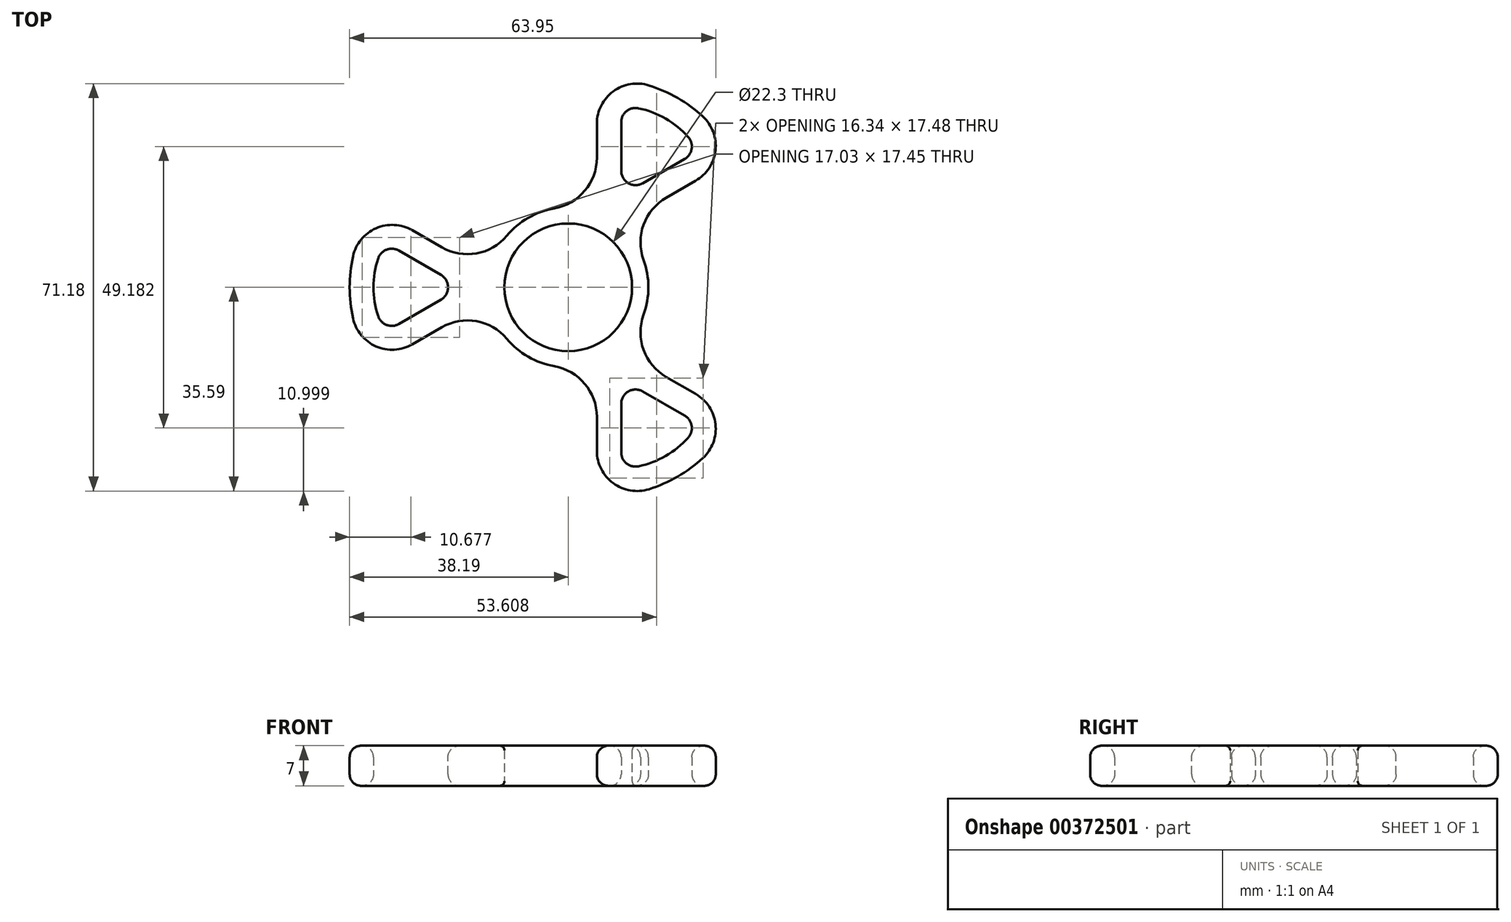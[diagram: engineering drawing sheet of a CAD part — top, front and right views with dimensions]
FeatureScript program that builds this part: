
annotation { "Feature Type Name" : "Feature", "Feature Type Description" : "" }
export const myFeature = defineFeature(function(context is Context, id is Id, definition is map)
    precondition{}
    {
        {
            var Q0;
            Q0=qCreatedBy(makeId("Top.planeOp"),FACE);
            var sketch = newSketch(context, id + "F0", { "sketchPlane" : qUnion([Q0])});
            skArc(sketch, "E0", {"start": v(-13.82, -2.2) * mm, "mid": v(-7, -12.12) * mm, "end": v(5, -13.08) * mm});
            skCircle(sketch, "E1.cCircle", {"center": v(-26, 0) * mm, "radius": 16 * mm, "construction": true});
            skLineSegment(sketch, "E1.0", {"start": v(-13.82, -2.2) * mm, "end": v(-34, -13.86) * mm});
            skLineSegment(sketch, "E1.2", {"start": v(-34, 13.86) * mm, "end": v(-13.82, 2.2) * mm});
            skPoint(sketch, "E2.orphan", {"position": v(-10, 0) * mm});
            skPoint(sketch, "E3.orphan", {"position": v(10, 0) * mm});
            skArc(sketch, "E4.trimOffspring", {"start": v(14, 0) * mm, "mid": v(12.64, 6.02) * mm, "end": v(8.82, 10.87) * mm});
            skArc(sketch, "E5", {"start": v(-34, 13.86) * mm, "mid": v(-38.2, 0) * mm, "end": v(-34, -13.86) * mm});
            skCircle(sketch, "E6", {"center": v(0, 0) * mm, "radius": 11.15 * mm});
            skCircle(sketch, "E7.cCircle", {"center": v(-27.5, 0) * mm, "radius": 9 * mm, "construction": true});
            skLineSegment(sketch, "E7.0", {"start": v(-18.5, 0) * mm, "end": v(-32, -7.8) * mm});
            skLineSegment(sketch, "E7.2", {"start": v(-32, 7.8) * mm, "end": v(-18.5, 0) * mm});
            skArc(sketch, "E8", {"start": v(-32, 7.8) * mm, "mid": v(-34.03, 0) * mm, "end": v(-32, -7.8) * mm});
            skLineSegment(sketch, "E9.1.0", {"start": v(9.25, -31.6) * mm, "end": v(9.25, -16.02) * mm});
            skCircle(sketch, "E9.1.1", {"center": v(13.75, -23.82) * mm, "radius": 9 * mm, "construction": true});
            skArc(sketch, "E9.1.2", {"start": v(9.25, -31.6) * mm, "mid": v(17.01, -29.47) * mm, "end": v(22.75, -23.82) * mm});
            skArc(sketch, "E9.1.3", {"start": v(5, -36.37) * mm, "mid": v(19.1, -33.07) * mm, "end": v(29, -22.52) * mm});
            skLineSegment(sketch, "E9.1.4", {"start": v(9.25, -16.02) * mm, "end": v(22.75, -23.82) * mm});
            skLineSegment(sketch, "E9.1.5", {"start": v(5, -36.37) * mm, "end": v(5, -13.08) * mm});
            skLineSegment(sketch, "E9.1.6", {"start": v(8.82, -10.87) * mm, "end": v(29, -22.52) * mm});
            skCircle(sketch, "E9.1.7", {"center": v(13, -22.52) * mm, "radius": 16 * mm, "construction": true});
            skLineSegment(sketch, "E9.2.0", {"start": v(22.75, 23.82) * mm, "end": v(9.25, 16.02) * mm});
            skCircle(sketch, "E9.2.1", {"center": v(13.75, 23.82) * mm, "radius": 9 * mm, "construction": true});
            skArc(sketch, "E9.2.2", {"start": v(22.75, 23.82) * mm, "mid": v(17.01, 29.47) * mm, "end": v(9.25, 31.6) * mm});
            skArc(sketch, "E9.2.3", {"start": v(29, 22.52) * mm, "mid": v(19.1, 33.07) * mm, "end": v(5, 36.37) * mm});
            skLineSegment(sketch, "E9.2.4", {"start": v(9.25, 16.02) * mm, "end": v(9.25, 31.6) * mm});
            skLineSegment(sketch, "E9.2.5", {"start": v(29, 22.52) * mm, "end": v(8.82, 10.87) * mm});
            skLineSegment(sketch, "E9.2.6", {"start": v(5, 13.08) * mm, "end": v(5, 36.37) * mm});
            skCircle(sketch, "E9.2.7", {"center": v(13, 22.52) * mm, "radius": 16 * mm, "construction": true});
            skArc(sketch, "E10.trimOffspring", {"start": v(5, 13.08) * mm, "mid": v(-7, 12.12) * mm, "end": v(-13.82, 2.2) * mm});
            skArc(sketch, "E11.trimOffspring", {"start": v(8.82, -10.87) * mm, "mid": v(12.64, -6.02) * mm, "end": v(14, 0) * mm});
            skSolve(sketch);
        }
        {
            var Q0;
            Q0=qSketchRegion(id+"F0",true);
            extrude(context, id + "F1", {"entities" : qUnion([Q0]), "depth" : 7 * mm});
        }
        {
            var Q0;
            Q0=makeQuery(id+"F1.opExtrude","SWEPT_EDGE",EDGE,{"disambiguationData":[OSD([sQuery(id+"F0.wireOp",EDGE,"E0"),sQuery(id+"F0.wireOp",EDGE,"E1.0")])]});
            var Q1;
            Q1=makeQuery(id+"F1.opExtrude","SWEPT_EDGE",EDGE,{"disambiguationData":[OSD([sQuery(id+"F0.wireOp",EDGE,"E0"),sQuery(id+"F0.wireOp",EDGE,"E9.1.5")])]});
            var Q2;
            Q2=makeQuery(id+"F1.opExtrude","SWEPT_EDGE",EDGE,{"disambiguationData":[OSD([sQuery(id+"F0.wireOp",EDGE,"E9.1.6"),sQuery(id+"F0.wireOp",EDGE,"E11.trimOffspring")])]});
            var Q3;
            Q3=makeQuery(id+"F1.opExtrude","SWEPT_EDGE",EDGE,{"disambiguationData":[OSD([sQuery(id+"F0.wireOp",EDGE,"E4.trimOffspring"),sQuery(id+"F0.wireOp",EDGE,"E9.2.5")])]});
            var Q4;
            Q4=makeQuery(id+"F1.opExtrude","SWEPT_EDGE",EDGE,{"disambiguationData":[OSD([sQuery(id+"F0.wireOp",EDGE,"E9.2.6"),sQuery(id+"F0.wireOp",EDGE,"E10.trimOffspring")])]});
            var Q5;
            Q5=makeQuery(id+"F1.opExtrude","SWEPT_EDGE",EDGE,{"disambiguationData":[OSD([sQuery(id+"F0.wireOp",EDGE,"E1.2"),sQuery(id+"F0.wireOp",EDGE,"E10.trimOffspring")])]});
            fillet(context, id + "F2", {"entities" : qUnion([Q0, Q1, Q2, Q3, Q4, Q5]), "radius" : 9 * mm, "tangentPropagation" : true, "allowEdgeOverflow" : false});
        }
        {
            var Q0;
            Q0=makeQuery(id+"F1.opExtrude","SWEPT_EDGE",EDGE,{"disambiguationData":[OSD([sQuery(id+"F0.wireOp",EDGE,"E9.1.3"),sQuery(id+"F0.wireOp",EDGE,"E9.1.6")])]});
            var Q1;
            Q1=makeQuery(id+"F1.opExtrude","SWEPT_EDGE",EDGE,{"disambiguationData":[OSD([sQuery(id+"F0.wireOp",EDGE,"E9.2.3"),sQuery(id+"F0.wireOp",EDGE,"E9.2.5")])]});
            var Q2;
            Q2=makeQuery(id+"F1.opExtrude","SWEPT_EDGE",EDGE,{"disambiguationData":[OSD([sQuery(id+"F0.wireOp",EDGE,"E9.2.3"),sQuery(id+"F0.wireOp",EDGE,"E9.2.6")])]});
            var Q3;
            Q3=makeQuery(id+"F1.opExtrude","SWEPT_EDGE",EDGE,{"disambiguationData":[OSD([sQuery(id+"F0.wireOp",EDGE,"E1.2"),sQuery(id+"F0.wireOp",EDGE,"E5")])]});
            var Q4;
            Q4=makeQuery(id+"F1.opExtrude","SWEPT_EDGE",EDGE,{"disambiguationData":[OSD([sQuery(id+"F0.wireOp",EDGE,"E1.0"),sQuery(id+"F0.wireOp",EDGE,"E5")])]});
            var Q5;
            Q5=makeQuery(id+"F1.opExtrude","SWEPT_EDGE",EDGE,{"disambiguationData":[OSD([sQuery(id+"F0.wireOp",EDGE,"E9.1.3"),sQuery(id+"F0.wireOp",EDGE,"E9.1.5")])]});
            fillet(context, id + "F3", {"entities" : qUnion([Q0, Q1, Q2, Q3, Q4, Q5]), "radius" : 7 * mm, "tangentPropagation" : true, "defaultsChanged" : true, "vertexSettings" : [], "allowEdgeOverflow" : false});
        }
        {
            var Q0;
            Q0=makeQuery(id+"F1.opExtrude","SWEPT_EDGE",EDGE,{"disambiguationData":[OSD([sQuery(id+"F0.wireOp",EDGE,"E7.2"),sQuery(id+"F0.wireOp",EDGE,"E8")])]});
            var Q1;
            Q1=makeQuery(id+"F1.opExtrude","SWEPT_EDGE",EDGE,{"disambiguationData":[OSD([sQuery(id+"F0.wireOp",EDGE,"E7.0"),sQuery(id+"F0.wireOp",EDGE,"E7.2")])]});
            var Q2;
            Q2=makeQuery(id+"F1.opExtrude","SWEPT_EDGE",EDGE,{"disambiguationData":[OSD([sQuery(id+"F0.wireOp",EDGE,"E7.0"),sQuery(id+"F0.wireOp",EDGE,"E8")])]});
            var Q3;
            Q3=makeQuery(id+"F1.opExtrude","SWEPT_EDGE",EDGE,{"disambiguationData":[OSD([sQuery(id+"F0.wireOp",EDGE,"E9.1.0"),sQuery(id+"F0.wireOp",EDGE,"E9.1.2")])]});
            var Q4;
            Q4=makeQuery(id+"F1.opExtrude","SWEPT_EDGE",EDGE,{"disambiguationData":[OSD([sQuery(id+"F0.wireOp",EDGE,"E9.1.0"),sQuery(id+"F0.wireOp",EDGE,"E9.1.4")])]});
            var Q5;
            Q5=makeQuery(id+"F1.opExtrude","SWEPT_EDGE",EDGE,{"disambiguationData":[OSD([sQuery(id+"F0.wireOp",EDGE,"E9.1.2"),sQuery(id+"F0.wireOp",EDGE,"E9.1.4")])]});
            var Q6;
            Q6=makeQuery(id+"F1.opExtrude","SWEPT_EDGE",EDGE,{"disambiguationData":[OSD([sQuery(id+"F0.wireOp",EDGE,"E9.2.0"),sQuery(id+"F0.wireOp",EDGE,"E9.2.4")])]});
            var Q7;
            Q7=makeQuery(id+"F1.opExtrude","SWEPT_EDGE",EDGE,{"disambiguationData":[OSD([sQuery(id+"F0.wireOp",EDGE,"E9.2.2"),sQuery(id+"F0.wireOp",EDGE,"E9.2.4")])]});
            var Q8;
            Q8=makeQuery(id+"F1.opExtrude","SWEPT_EDGE",EDGE,{"disambiguationData":[OSD([sQuery(id+"F0.wireOp",EDGE,"E9.2.0"),sQuery(id+"F0.wireOp",EDGE,"E9.2.2")])]});
            fillet(context, id + "F4", {"entities" : qUnion([Q0, Q1, Q2, Q3, Q4, Q5, Q6, Q7, Q8]), "radius" : 2.5 * mm, "tangentPropagation" : true, "defaultsChanged" : true, "vertexSettings" : [], "allowEdgeOverflow" : false});
        }
        {
            var Q0;
            Q0=makeQuery(id+"F1.opExtrude","SWEPT_FACE",FACE,{"disambiguationData":[OSD([sQuery(id+"F0.wireOp",EDGE,"E6")])]});
            fillet(context, id + "F5", {"entities" : qUnion([Q0]), "radius" : .8 * mm, "tangentPropagation" : true, "allowEdgeOverflow" : false});
        }
        {
            var Q0;
            Q0=makeQuery(id+"F1.opExtrude","CAP_FACE",FACE,{"disambiguationData":[OSD([sQuery(id+"F0.wireOp",EDGE,"E0"),sQuery(id+"F0.wireOp",EDGE,"E1.0"),sQuery(id+"F0.wireOp",EDGE,"E1.2"),sQuery(id+"F0.wireOp",EDGE,"E4.trimOffspring"),sQuery(id+"F0.wireOp",EDGE,"E5"),sQuery(id+"F0.wireOp",EDGE,"E6"),sQuery(id+"F0.wireOp",EDGE,"E7.0"),sQuery(id+"F0.wireOp",EDGE,"E7.2"),sQuery(id+"F0.wireOp",EDGE,"E8"),sQuery(id+"F0.wireOp",EDGE,"E9.1.0"),sQuery(id+"F0.wireOp",EDGE,"E9.1.2"),sQuery(id+"F0.wireOp",EDGE,"E9.1.3"),sQuery(id+"F0.wireOp",EDGE,"E9.1.4"),sQuery(id+"F0.wireOp",EDGE,"E9.1.5"),sQuery(id+"F0.wireOp",EDGE,"E9.1.6"),sQuery(id+"F0.wireOp",EDGE,"E9.2.0"),sQuery(id+"F0.wireOp",EDGE,"E9.2.2"),sQuery(id+"F0.wireOp",EDGE,"E9.2.3"),sQuery(id+"F0.wireOp",EDGE,"E9.2.4"),sQuery(id+"F0.wireOp",EDGE,"E9.2.5"),sQuery(id+"F0.wireOp",EDGE,"E9.2.6"),sQuery(id+"F0.wireOp",EDGE,"E10.trimOffspring"),sQuery(id+"F0.wireOp",EDGE,"E11.trimOffspring")])],"isStart":false});
            var Q1;
            Q1=makeQuery(id+"F1.opExtrude","CAP_FACE",FACE,{"disambiguationData":[OSD([sQuery(id+"F0.wireOp",EDGE,"E0"),sQuery(id+"F0.wireOp",EDGE,"E1.0"),sQuery(id+"F0.wireOp",EDGE,"E1.2"),sQuery(id+"F0.wireOp",EDGE,"E4.trimOffspring"),sQuery(id+"F0.wireOp",EDGE,"E5"),sQuery(id+"F0.wireOp",EDGE,"E6"),sQuery(id+"F0.wireOp",EDGE,"E7.0"),sQuery(id+"F0.wireOp",EDGE,"E7.2"),sQuery(id+"F0.wireOp",EDGE,"E8"),sQuery(id+"F0.wireOp",EDGE,"E9.1.0"),sQuery(id+"F0.wireOp",EDGE,"E9.1.2"),sQuery(id+"F0.wireOp",EDGE,"E9.1.3"),sQuery(id+"F0.wireOp",EDGE,"E9.1.4"),sQuery(id+"F0.wireOp",EDGE,"E9.1.5"),sQuery(id+"F0.wireOp",EDGE,"E9.1.6"),sQuery(id+"F0.wireOp",EDGE,"E9.2.0"),sQuery(id+"F0.wireOp",EDGE,"E9.2.2"),sQuery(id+"F0.wireOp",EDGE,"E9.2.3"),sQuery(id+"F0.wireOp",EDGE,"E9.2.4"),sQuery(id+"F0.wireOp",EDGE,"E9.2.5"),sQuery(id+"F0.wireOp",EDGE,"E9.2.6"),sQuery(id+"F0.wireOp",EDGE,"E10.trimOffspring"),sQuery(id+"F0.wireOp",EDGE,"E11.trimOffspring")])],"isStart":true});
            fillet(context, id + "F6", {"entities" : qUnion([Q0, Q1]), "radius" : 2 * mm, "tangentPropagation" : true, "allowEdgeOverflow" : false});
        }
    });
